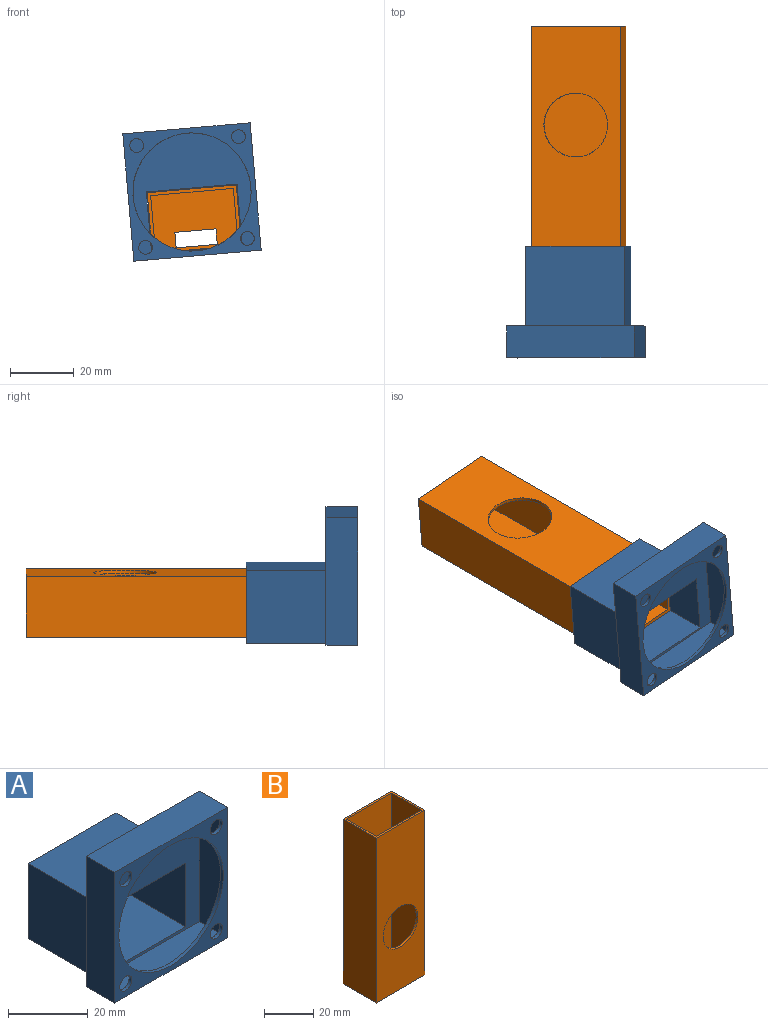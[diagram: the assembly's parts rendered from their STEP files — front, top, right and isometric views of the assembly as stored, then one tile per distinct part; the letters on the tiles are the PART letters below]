
ASSEMBLY  parts=2 mates=1
PART A: 25 faces, bbox 40x35x40 mm
  f0: plane 31x23mm, normal (0,1,0), area 157.2mm2, adj f6,f18,f19,f20,f21,f22,f23,f24
  f1: plane 40x40mm, normal (0,1,0), area 887mm2, adj f2,f4,f5,f6,f18,f19,f20
  f2: plane 40x10mm, normal (-1,0,0), area 400mm2, adj f1,f3,f5,f6
  f3: plane 40x40mm, normal (0,-1,0), area 466.7mm2, adj f2,f4,f5,f6,f7,f14,f15,f16
  f4: plane 40x10mm, normal (1,0,0), area 400mm2, adj f1,f3,f5,f6
  f5: plane 40x10mm, normal (0,0,1), area 400mm2, adj f1,f2,f3,f4
  f6: plane 40x35mm, normal (0,0,-1), area 1175mm2, adj f0,f1,f2,f3,f4,f18,f20
  f7: cylinder r=18.5mm len=37mm, axis (0,-1,0), area 116.2mm2, adj f3,f11
  f8: plane 38x8mm, normal (0,0,-1), area 304mm2, adj f9,f10,f11,f12
  f9: plane 38x38mm, normal (0,-1,0), area 888.2mm2, adj f8,f10,f12,f13,f21,f22,f23,f24
  f10: plane 38x8mm, normal (1,0,0), area 304mm2, adj f8,f9,f11,f13
  f11: plane 38x38mm, normal (0,1,0), area 310.7mm2, adj f7,f8,f10,f12,f13,f14,f15,f16
  f12: plane 38x8mm, normal (-1,0,0), area 304mm2, adj f8,f9,f11,f13
  f13: plane 38x8mm, normal (0,0,1), area 304mm2, adj f9,f10,f11,f12
  f14: cylinder r=2.15mm len=4.3mm, axis (0,-1,0), area 13.5mm2, adj f3,f11
  f15: cylinder r=2.15mm len=4.3mm, axis (0,-1,0), area 13.5mm2, adj f3,f11
  f16: cylinder r=2.15mm len=4.3mm, axis (0,-1,0), area 13.5mm2, adj f3,f11
  f17: cylinder r=2.15mm len=4.3mm, axis (0,-1,0), area 13.5mm2, adj f3,f11
  f18: plane 25x23mm, normal (-1,0,0), area 575mm2, adj f0,f1,f6,f19
  f19: plane 31x25mm, normal (0,0,1), area 775mm2, adj f0,f1,f18,f20
  f20: plane 25x23mm, normal (1,0,0), area 575mm2, adj f0,f1,f6,f19
  f21: plane 26x19.5mm, normal (1,0,0), area 507mm2, adj f0,f9,f22,f24
  f22: plane 28.5x26mm, normal (0,0,-1), area 741mm2, adj f0,f9,f21,f23
  f23: plane 26x19.5mm, normal (-1,0,0), area 507mm2, adj f0,f9,f22,f24
  f24: plane 28.5x26mm, normal (0,0,1), area 741mm2, adj f0,f9,f21,f23
PART B: 15 faces, bbox 28x19x82 mm
  f0: plane 81x17mm, normal (-1,0,0), area 1377mm2, adj f1,f6,f8,f13
  f1: plane 82x26mm, normal (0,-1,0), area 2118.9mm2, adj f0,f5,f8,f9,f10,f12,f13
  f2: plane 82x28mm, normal (0,1,0), area 2296mm2, adj f3,f7,f8,f9
  f3: plane 82x19mm, normal (-1,0,0), area 1558mm2, adj f2,f4,f8,f9
  f4: plane 82x28mm, normal (0,-1,0), area 1981.8mm2, adj f3,f7,f8,f9,f14
  f5: plane 81x17mm, normal (1,0,0), area 1377mm2, adj f1,f6,f8,f13
  f6: plane 81x26mm, normal (0,1,0), area 1791.8mm2, adj f0,f5,f8,f13,f14
  f7: plane 82x19mm, normal (1,0,0), area 1558mm2, adj f2,f4,f8,f9
  f8: plane 28x19mm, normal (0,0,1), area 90mm2, adj f0,f1,f2,f3,f4,f5,f6,f7
  f9: plane 28x19mm, normal (0,0,-1), area 469.2mm2, adj f1,f2,f3,f4,f7,f10,f11,f12
  f10: plane 4.86x1mm, normal (-1,0,0), area 4.9mm2, adj f1,f9,f11,f13
  f11: plane 12.92x1mm, normal (0,1,0), area 12.9mm2, adj f9,f10,f12,f13
  f12: plane 4.86x1mm, normal (1,0,0), area 4.9mm2, adj f1,f9,f11,f13
  f13: plane 26x17mm, normal (0,0,1), area 379.2mm2, adj f0,f1,f5,f6,f10,f11,f12
  f14: cylinder r=10mm len=20mm, axis (0,-1,0), area 62.8mm2, adj f4,f6
PLACE A rot(axis=(0,-1,0),5deg) t=(-57.97,-36.62,-8.3)mm
PLACE B rot(axis=(0.03,0.71,-0.71),176.5deg) t=(-58.97,62.26,3.15)mm
MATE slider B.f8 <-> A.f0  axis (0,-1,0) through (-58.97,-19.74,3.15)mm
